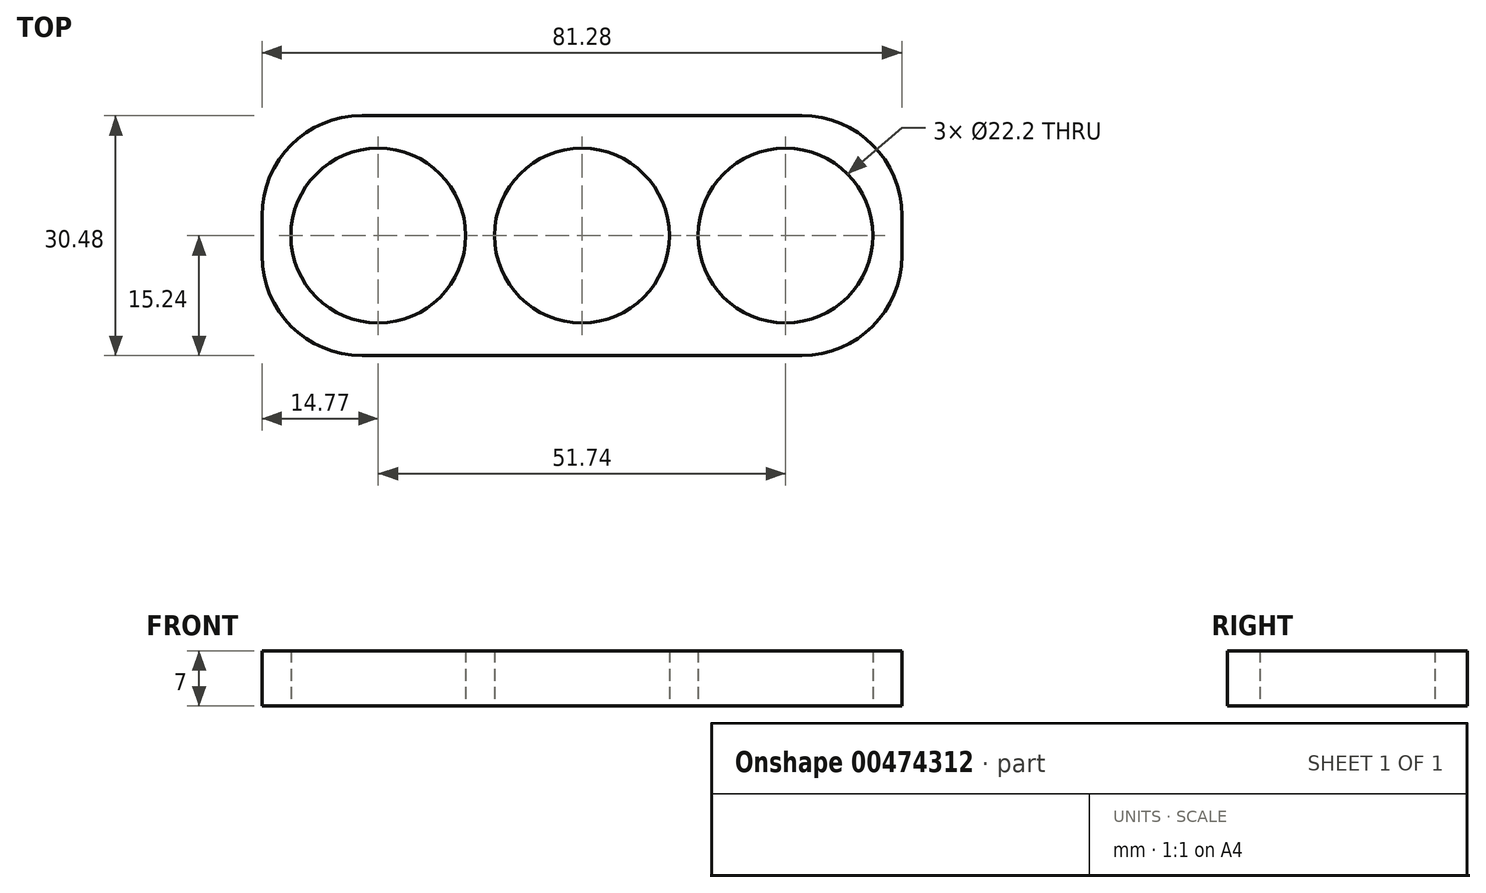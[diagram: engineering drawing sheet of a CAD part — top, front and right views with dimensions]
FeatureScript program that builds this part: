
annotation { "Feature Type Name" : "Feature", "Feature Type Description" : "" }
export const myFeature = defineFeature(function(context is Context, id is Id, definition is map)
    precondition{}
    {
        {
            var Q0;
            Q0=qCreatedBy(makeId("Top.planeOp"),FACE);
            var sketch = newSketch(context, id + "F0", { "sketchPlane" : qUnion([Q0])});
            skCircle(sketch, "E0", {"center": v(0, 0) * mm, "radius": 11.1 * mm});
            skLineSegment(sketch, "E1.bottom", {"start": v(40.64, -15.24) * mm, "end": v(-40.64, -15.24) * mm});
            skLineSegment(sketch, "E1.top", {"start": v(40.64, 15.24) * mm, "end": v(-40.64, 15.24) * mm});
            skLineSegment(sketch, "E1.left", {"start": v(40.64, -15.24) * mm, "end": v(40.64, 15.24) * mm});
            skLineSegment(sketch, "E1.right", {"start": v(-40.64, -15.24) * mm, "end": v(-40.64, 15.24) * mm});
            skLineSegment(sketch, "E2", {"start": v(-11.1, 0) * mm, "end": v(-40.64, 0) * mm});
            skLineSegment(sketch, "E3", {"start": v(11.1, 0) * mm, "end": v(40.64, 0) * mm});
            skCircle(sketch, "E4", {"center": v(-25.87, 0) * mm, "radius": 11.1 * mm});
            skCircle(sketch, "E5", {"center": v(25.87, 0) * mm, "radius": 11.1 * mm});
            skSolve(sketch);
        }
        {
            var Q0;
            {var subQ1=sQuery(id+"F0.wireOp",EDGE,"E1.top");Q0=makeQuery(id+"F0.imprint","IMPRINT",FACE,{"disambiguationData":[TD([[makeQuery(id+"F0.imprint","IMPRINT",EDGE,{"derivedFrom":subQ1}),1.0]])]});}
            var Q1;
            {var subQ1=sQuery(id+"F0.wireOp",EDGE,"E1.bottom");Q1=makeQuery(id+"F0.imprint","IMPRINT",FACE,{"disambiguationData":[TD([[makeQuery(id+"F0.imprint","IMPRINT",EDGE,{"derivedFrom":subQ1}),-1.0]])]});}
            extrude(context, id + "F1", {"entities" : qUnion([Q0, Q1]), "depth" : 7 * mm});
        }
        {
            var Q0;
            Q0=makeQuery(id+"F1.opExtrude","SWEPT_EDGE",EDGE,{"disambiguationData":[OSD([sQuery(id+"F0.wireOp",EDGE,"E1.top"),sQuery(id+"F0.wireOp",EDGE,"E1.left")])]});
            var Q1;
            Q1=makeQuery(id+"F1.opExtrude","SWEPT_EDGE",EDGE,{"disambiguationData":[OSD([sQuery(id+"F0.wireOp",EDGE,"E1.bottom"),sQuery(id+"F0.wireOp",EDGE,"E1.left")])]});
            var Q2;
            Q2=makeQuery(id+"F1.opExtrude","SWEPT_EDGE",EDGE,{"disambiguationData":[OSD([sQuery(id+"F0.wireOp",EDGE,"E1.top"),sQuery(id+"F0.wireOp",EDGE,"E1.right")])]});
            var Q3;
            Q3=makeQuery(id+"F1.opExtrude","SWEPT_EDGE",EDGE,{"disambiguationData":[OSD([sQuery(id+"F0.wireOp",EDGE,"E1.bottom"),sQuery(id+"F0.wireOp",EDGE,"E1.right")])]});
            fillet(context, id + "F2", {"entities" : qUnion([Q0, Q1, Q2, Q3]), "radius" : 12.7 * mm, "tangentPropagation" : true, "allowEdgeOverflow" : false});
        }
    });
